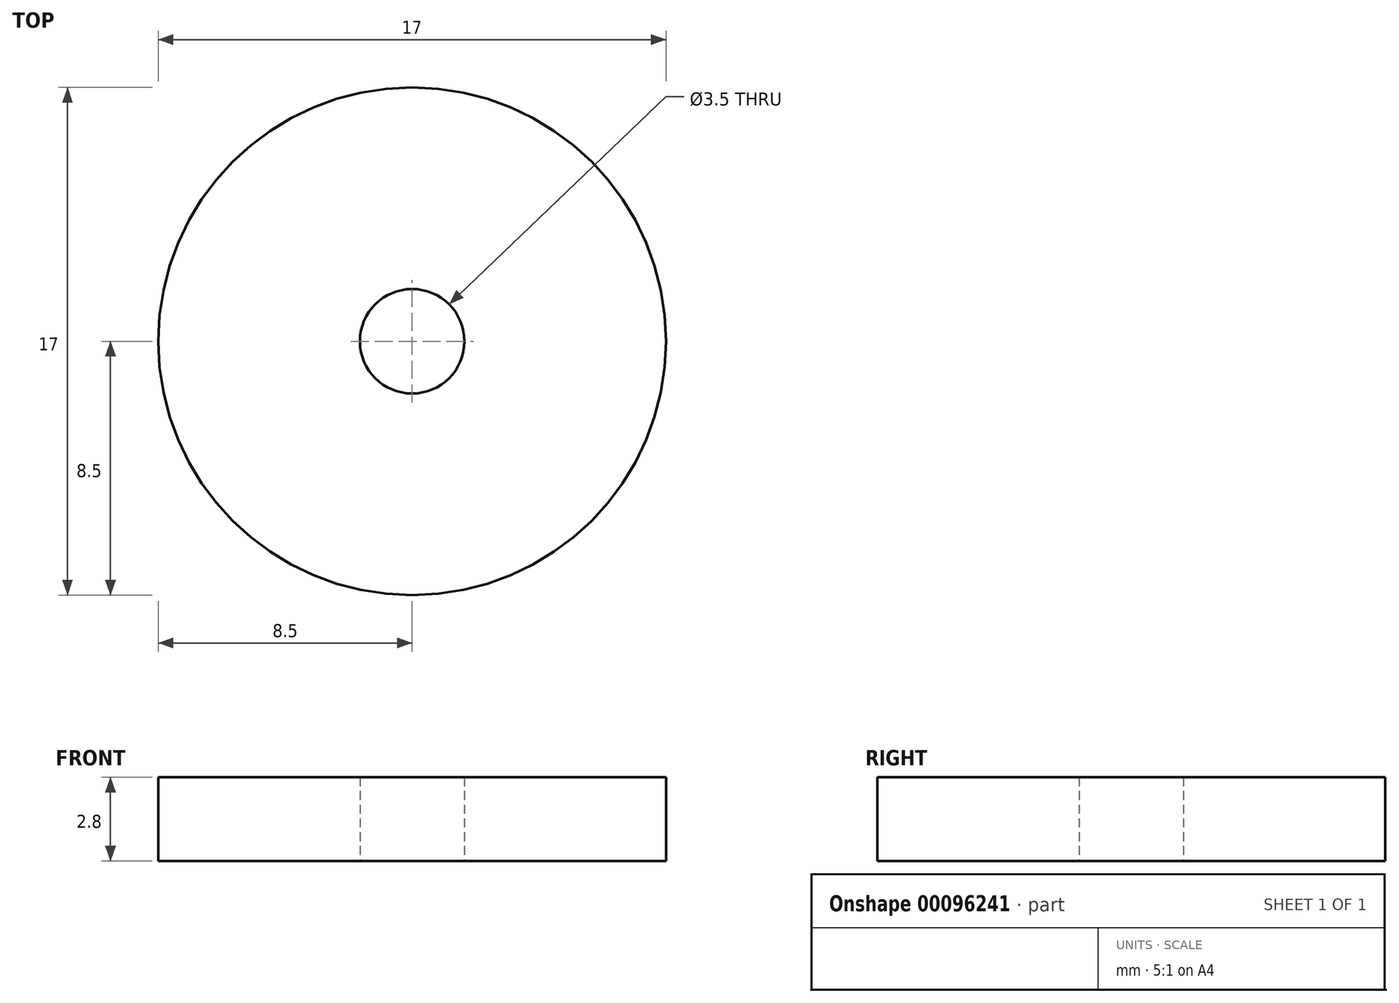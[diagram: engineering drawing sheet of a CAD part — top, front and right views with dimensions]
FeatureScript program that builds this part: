
annotation { "Feature Type Name" : "Feature", "Feature Type Description" : "" }
export const myFeature = defineFeature(function(context is Context, id is Id, definition is map)
    precondition{}
    {
        {
            var Q0;
            Q0=qCreatedBy(makeId("Top.planeOp"),FACE);
            var sketch = newSketch(context, id + "F0", { "sketchPlane" : qUnion([Q0])});
            skCircle(sketch, "E0", {"center": v(0, 0) * mm, "radius": 8.5 * mm});
            skCircle(sketch, "E1", {"center": v(0, 0) * mm, "radius": 1.75 * mm});
            skSolve(sketch);
        }
        {
            var Q0;
            Q0=makeQuery(id+"F0.imprint","IMPRINT",FACE,{"disambiguationData":[TD([[makeQuery(id+"F0.imprint","IMPRINT",EDGE,{"derivedFrom":sQuery(id+"F0.wireOp",EDGE,"E0")}),1.0]])]});
            extrude(context, id + "F1", {"entities" : qUnion([Q0]), "depth" : 2.8 * mm});
        }
    });
